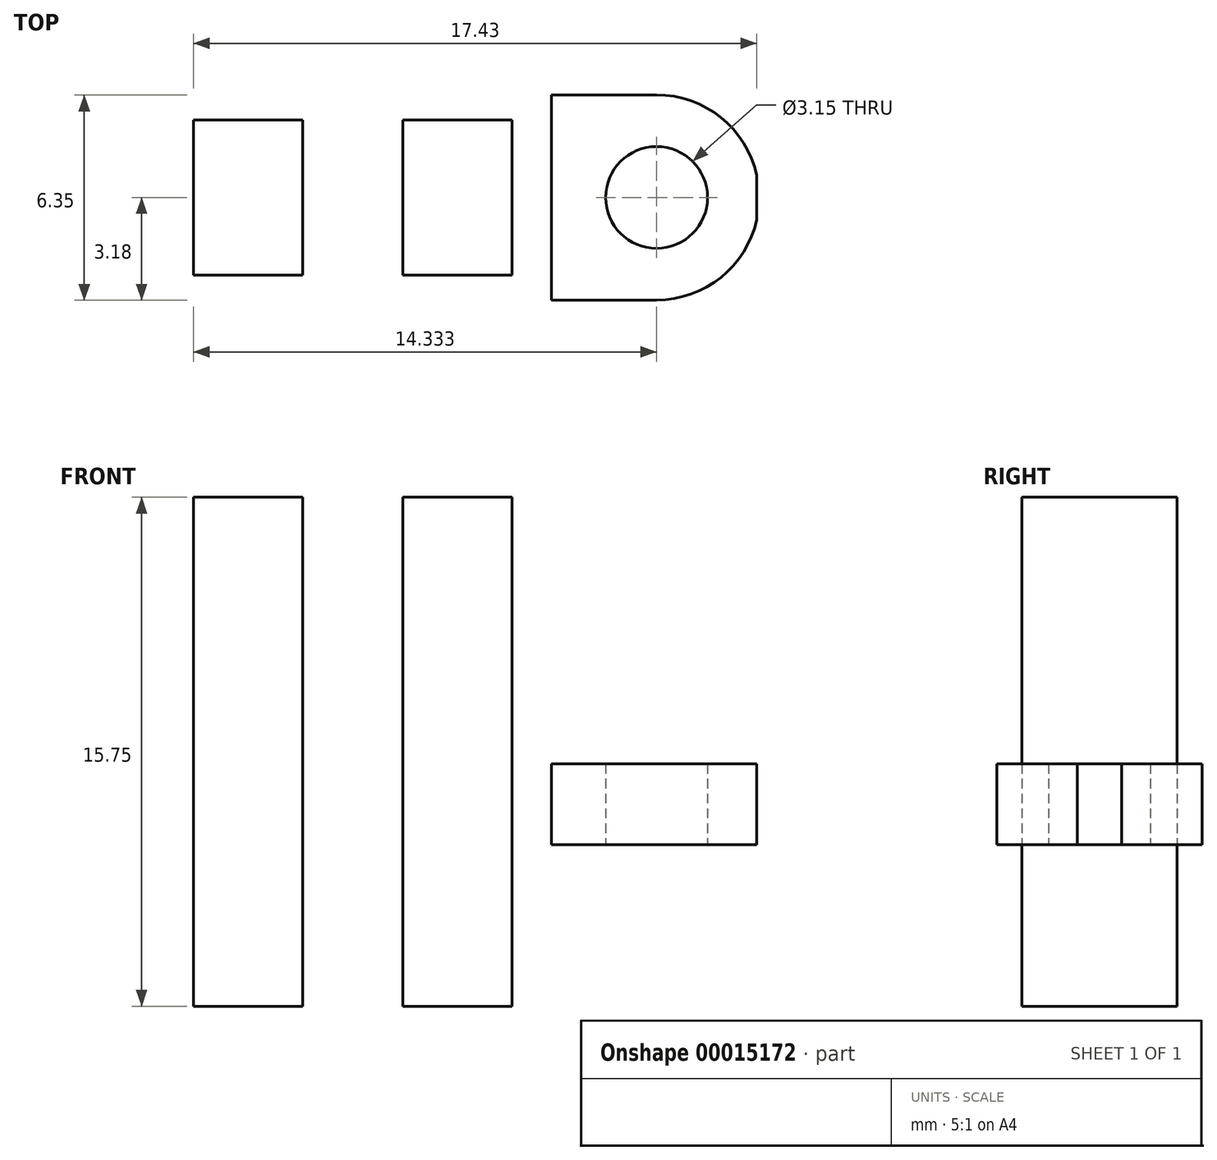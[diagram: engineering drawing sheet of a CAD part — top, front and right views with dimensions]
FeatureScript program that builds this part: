
annotation { "Feature Type Name" : "Feature", "Feature Type Description" : "" }
export const myFeature = defineFeature(function(context is Context, id is Id, definition is map)
    precondition{}
    {
        {
            var Q0;
            Q0=qCreatedBy(makeId("Top.planeOp"),FACE);
            var sketch = newSketch(context, id + "F0", { "sketchPlane" : qUnion([Q0])});
            skLineSegment(sketch, "E0.bottom", {"start": v(-10.05, 3.17) * mm, "end": v(5.5, 3.17) * mm});
            skLineSegment(sketch, "E0.top", {"start": v(-10.05, -3.17) * mm, "end": v(5.5, -3.17) * mm});
            skLineSegment(sketch, "E0.left", {"start": v(-10.05, 3.17) * mm, "end": v(-10.05, -3.17) * mm});
            skLineSegment(sketch, "E0.right", {"start": v(8.6, 0.69) * mm, "end": v(8.6, -0.69) * mm});
            skPoint(sketch, "E1", {"position": v(-10.05, 0) * mm});
            skLineSegment(sketch, "E2.bottom", {"start": v(-10.05, 3.17) * mm, "end": v(-5.45, 3.17) * mm});
            skLineSegment(sketch, "E2.top", {"start": v(-10.05, -3.17) * mm, "end": v(-5.45, -3.17) * mm});
            skLineSegment(sketch, "E2.right", {"start": v(-5.45, 3.17) * mm, "end": v(-5.45, -3.17) * mm});
            skLineSegment(sketch, "E3.bottom", {"start": v(-2.35, 3.17) * mm, "end": v(2.25, 3.17) * mm});
            skLineSegment(sketch, "E3.top", {"start": v(-2.35, -3.17) * mm, "end": v(2.25, -3.17) * mm});
            skLineSegment(sketch, "E3.left", {"start": v(-2.35, 3.17) * mm, "end": v(-2.35, -3.17) * mm});
            skLineSegment(sketch, "E3.right", {"start": v(2.25, 3.17) * mm, "end": v(2.25, -3.17) * mm});
            skPoint(sketch, "E4", {"position": v(5.5, 0) * mm});
            skPoint(sketch, "E4.positionSnap0", {"position": v(2.25, 0) * mm});
            skCircle(sketch, "E5", {"center": v(5.5, 0) * mm, "radius": 1.57 * mm});
            skArc(sketch, "E6", {"start": v(5.5, -3.17) * mm, "mid": v(8.68, 0) * mm, "end": v(5.5, 3.18) * mm});
            skLineSegment(sketch, "E7.bottom", {"start": v(-5.45, 2.4) * mm, "end": v(-8.83, 2.4) * mm});
            skLineSegment(sketch, "E7.top", {"start": v(-5.45, -2.4) * mm, "end": v(-8.83, -2.4) * mm});
            skLineSegment(sketch, "E7.left", {"start": v(-5.45, 2.4) * mm, "end": v(-5.45, -2.4) * mm});
            skLineSegment(sketch, "E7.right", {"start": v(-8.83, 2.4) * mm, "end": v(-8.83, -2.4) * mm});
            skLineSegment(sketch, "E8.bottom", {"start": v(-2.35, 2.4) * mm, "end": v(1.03, 2.4) * mm});
            skLineSegment(sketch, "E8.top", {"start": v(-2.35, -2.4) * mm, "end": v(1.03, -2.4) * mm});
            skLineSegment(sketch, "E8.left", {"start": v(-2.35, 2.4) * mm, "end": v(-2.35, -2.4) * mm});
            skLineSegment(sketch, "E8.right", {"start": v(1.03, 2.4) * mm, "end": v(1.03, -2.4) * mm});
            skPoint(sketch, "E9", {"position": v(-5.45, 0) * mm});
            skSolve(sketch);
        }
        {
            var Q0;
            {var subQ1=sQuery(id+"F0.wireOp",EDGE,"E2.bottom");Q0=makeQuery(id+"F0.imprint","IMPRINT",FACE,{"disambiguationData":[TD([[makeQuery(id+"F0.imprint","IMPRINT",EDGE,{"derivedFrom":subQ1}),-1.0]])]});}
            var Q1;
            {var subQ3=sQuery(id+"F0.wireOp",EDGE,"E7.left");Q1=makeQuery(id+"F0.imprint","IMPRINT",FACE,{"disambiguationData":[TD([[makeQuery(id+"F0.imprint","IMPRINT",EDGE,{"derivedFrom":subQ3}),1.0]])]});}
            var Q2;
            {var subQ4=sQuery(id+"F0.wireOp",EDGE,"E3.bottom");Q2=makeQuery(id+"F0.imprint","IMPRINT",FACE,{"disambiguationData":[TD([[makeQuery(id+"F0.imprint","IMPRINT",EDGE,{"derivedFrom":subQ4}),-1.0]])]});}
            var Q3;
            {var subQ4=sQuery(id+"F0.wireOp",EDGE,"E0.right");Q3=makeQuery(id+"F0.imprint","IMPRINT",FACE,{"disambiguationData":[TD([[makeQuery(id+"F0.imprint","IMPRINT",EDGE,{"derivedFrom":subQ4}),-1.0]])]});}
            extrude(context, id + "F1", {"entities" : qUnion([Q0, Q1, Q2, Q3]), "depth" : 2.5 * mm});
        }
        {
            var Q0;
            Q0=makeQuery(id+"F0.imprint","IMPRINT",FACE,{"disambiguationData":[TD([[makeQuery(id+"F0.imprint","IMPRINT",EDGE,{"derivedFrom":sQuery(id+"F0.wireOp",EDGE,"E7.bottom")}),1.0]])]});
            var Q1;
            Q1=makeQuery(id+"F0.imprint","IMPRINT",FACE,{"disambiguationData":[TD([[makeQuery(id+"F0.imprint","IMPRINT",EDGE,{"derivedFrom":sQuery(id+"F0.wireOp",EDGE,"E8.bottom")}),-1.0]])]});
            var Q2;
            {var subQ1=sQuery(id+"F0.wireOp",EDGE,"E2.bottom");Q2=makeQuery(id+"F0.imprint","IMPRINT",FACE,{"disambiguationData":[TD([[makeQuery(id+"F0.imprint","IMPRINT",EDGE,{"derivedFrom":subQ1}),-1.0]])]});}
            var Q3;
            {var subQ4=sQuery(id+"F0.wireOp",EDGE,"E3.bottom");Q3=makeQuery(id+"F0.imprint","IMPRINT",FACE,{"disambiguationData":[TD([[makeQuery(id+"F0.imprint","IMPRINT",EDGE,{"derivedFrom":subQ4}),-1.0]])]});}
            extrude(context, id + "F2", {"entities" : qUnion([Q0, Q1, Q2, Q3]), "operationType" : NewBodyOperationType.ADD, "depth" : 10.75 * mm});
        }
        {
            var Q0;
            Q0=makeQuery(id+"F0.imprint","IMPRINT",FACE,{"disambiguationData":[TD([[makeQuery(id+"F0.imprint","IMPRINT",EDGE,{"derivedFrom":sQuery(id+"F0.wireOp",EDGE,"E7.bottom")}),1.0]])]});
            var Q1;
            Q1=makeQuery(id+"F0.imprint","IMPRINT",FACE,{"disambiguationData":[TD([[makeQuery(id+"F0.imprint","IMPRINT",EDGE,{"derivedFrom":sQuery(id+"F0.wireOp",EDGE,"E8.bottom")}),-1.0]])]});
            extrude(context, id + "F3", {"entities" : qUnion([Q0, Q1]), "operationType" : NewBodyOperationType.ADD, "oppositeDirection" : true, "depth" : 5 * mm});
        }
    });
